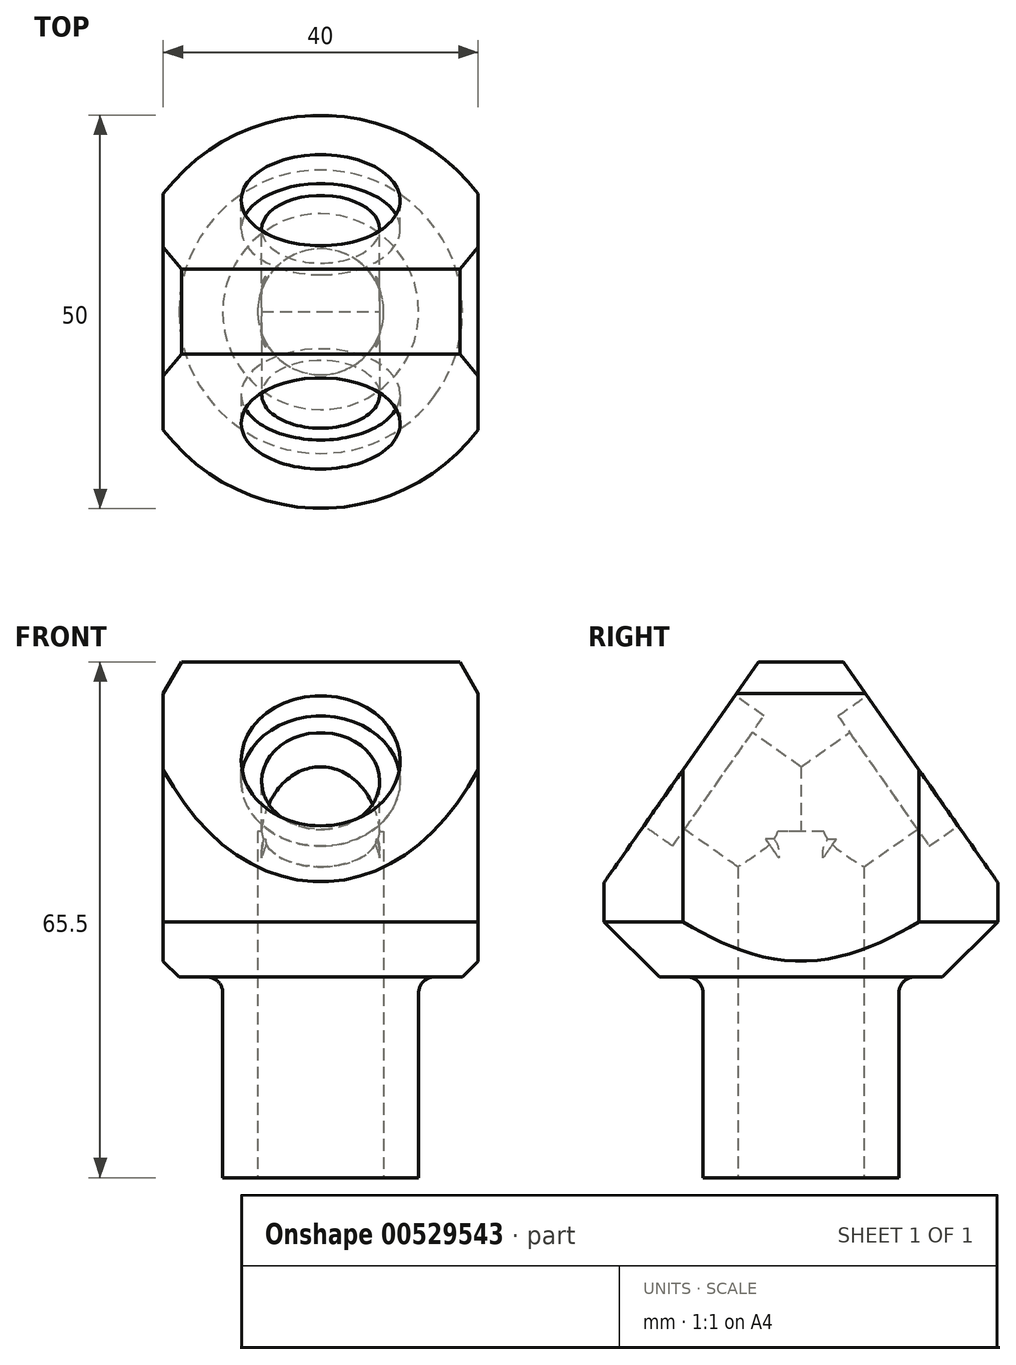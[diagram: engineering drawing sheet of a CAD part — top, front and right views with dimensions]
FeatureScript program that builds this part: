
annotation { "Feature Type Name" : "Feature", "Feature Type Description" : "" }
export const myFeature = defineFeature(function(context is Context, id is Id, definition is map)
    precondition{}
    {
        {
            var Q0;
            Q0=qCreatedBy(makeId("Top.planeOp"),FACE);
            var sketch = newSketch(context, id + "F0", { "sketchPlane" : qUnion([Q0])});
            skCircle(sketch, "E0", {"center": v(0, 0) * mm, "radius": 25 * mm});
            skSolve(sketch);
        }
        {
            var Q0;
            Q0 = qSketchRegion(id + "F0", true);
            extrude(context, id + "F1", {"entities" : qUnion([Q0]), "depth" : 65.5 * mm, "offsetDistance" : 25 * mm});
        }
        {
            var Q0;
            Q0=makeQuery(id+"F1.opExtrude","CAP_FACE",FACE,{"disambiguationData":[OSD([sQuery(id+"F0.wireOp",EDGE,"E0")])],"isStart":true});
            var sketch = newSketch(context, id + "F2", { "sketchPlane" : qUnion([Q0])});
            skCircle(sketch, "E1", {"center": v(0, 0) * mm, "radius": 8 * mm});
            skSolve(sketch);
        }
        {
            var Q0;
            Q0 = qSketchRegion(id + "F2", true);
            extrude(context, id + "F3", {"entities" : qUnion([Q0]), "operationType" : NewBodyOperationType.REMOVE, "oppositeDirection" : true, "depth" : 44 * mm, "offsetDistance" : 25 * mm});
        }
        {
            var Q0;
            Q0=qCreatedBy(makeId("Front.planeOp"),FACE);
            var sketch = newSketch(context, id + "F4", { "sketchPlane" : qUnion([Q0])});
            skLineSegment(sketch, "E2.bottom", {"start": v(37.7, 87.8) * mm, "end": v(20, 87.8) * mm});
            skLineSegment(sketch, "E2.top", {"start": v(37.7, 24) * mm, "end": v(20, 24) * mm});
            skLineSegment(sketch, "E2.left", {"start": v(37.7, 87.8) * mm, "end": v(37.7, 24) * mm});
            skLineSegment(sketch, "E2.right", {"start": v(20, 87.8) * mm, "end": v(20, 24) * mm});
            skLineSegment(sketch, "E3.bottom", {"start": v(-20, 73.43) * mm, "end": v(-40.98, 73.43) * mm});
            skLineSegment(sketch, "E3.top", {"start": v(-20, 24) * mm, "end": v(-40.98, 24) * mm});
            skLineSegment(sketch, "E3.left", {"start": v(-20, 73.43) * mm, "end": v(-20, 24) * mm});
            skLineSegment(sketch, "E3.right", {"start": v(-40.98, 73.43) * mm, "end": v(-40.98, 24) * mm});
            skSolve(sketch);
        }
        {
            var Q0;
            Q0 = qSketchRegion(id + "F4", true);
            extrude(context, id + "F5", {"entities" : qUnion([Q0]), "operationType" : NewBodyOperationType.REMOVE, "endBound" : BoundingType.SYMMETRIC, "oppositeDirection" : true, "depth" : 98.6 * mm, "offsetDistance" : 25 * mm});
        }
        {
            var Q0;
            Q0=makeQuery(id+"F5.boolean.opBoolean","INTERSECT",EDGE,{"derivedFrom":[makeQuery(id+"F1.opExtrude","CAP_FACE",FACE,{"disambiguationData":[OSD([sQuery(id+"F0.wireOp",EDGE,"E0")])],"isStart":false}),makeQuery(id+"F5.opExtrude","SWEPT_FACE",FACE,{"disambiguationData":[OSD([sQuery(id+"F4.wireOp",EDGE,"E2.right")])]})]});
            var Q1;
            Q1=makeQuery(id+"F5.boolean.opBoolean","INTERSECT",EDGE,{"derivedFrom":[makeQuery(id+"F1.opExtrude","CAP_FACE",FACE,{"disambiguationData":[OSD([sQuery(id+"F0.wireOp",EDGE,"E0")])],"isStart":false}),makeQuery(id+"F5.opExtrude","SWEPT_FACE",FACE,{"disambiguationData":[OSD([sQuery(id+"F4.wireOp",EDGE,"E3.left")])]})]});
            chamfer(context, id + "F6", {"entities" : qUnion([Q0, Q1]), "chamferType" : ChamferType.OFFSET_ANGLE, "width" : 4 * mm, "oppositeDirection" : false, "angle" : 30 * degree, "tangentPropagation" : true});
        }
        {
            var Q0;
            Q0=makeQuery(id+"F1.opExtrude","CAP_FACE",FACE,{"disambiguationData":[OSD([sQuery(id+"F0.wireOp",EDGE,"E0")])],"isStart":true});
            var sketch = newSketch(context, id + "F7", { "sketchPlane" : qUnion([Q0])});
            skCircle(sketch, "E4", {"center": v(0, 0) * mm, "radius": 12.45 * mm});
            skCircle(sketch, "E5", {"center": v(0, 0) * mm, "radius": 27.63 * mm});
            skSolve(sketch);
        }
        {
            var Q0;
            Q0 = qSketchRegion(id + "F7", true);
            extrude(context, id + "F8", {"entities" : qUnion([Q0]), "operationType" : NewBodyOperationType.REMOVE, "oppositeDirection" : true, "depth" : 25.5 * mm, "offsetDistance" : 25 * mm});
        }
        {
            var Q0;
            Q0=makeQuery(id+"F8.boolean.opBoolean","COPY",EDGE,{"derivedFrom":makeQuery(id+"F8.opExtrude","CAP_EDGE",EDGE,{"disambiguationData":[OSD([sQuery(id+"F7.wireOp",EDGE,"E4")])],"isStart":false})});
            fillet(context, id + "F9", {"entities" : qUnion([Q0]), "radius" : 2 * mm, "tangentPropagation" : true, "allowEdgeOverflow" : false});
        }
        {
            var Q0;
            Q0=qCreatedBy(makeId("Right.planeOp"),FACE);
            var sketch = newSketch(context, id + "F10", { "sketchPlane" : qUnion([Q0])});
            skLineSegment(sketch, "E6", {"start": v(14, 53.2) * mm, "end": v(2.8, 69.22) * mm});
            skLineSegment(sketch, "E7", {"start": v(2.8, 69.22) * mm, "end": v(27.83, 33.47) * mm});
            skLineSegment(sketch, "E8", {"start": v(27.83, 33.47) * mm, "end": v(27.83, 71.21) * mm});
            skLineSegment(sketch, "E9", {"start": v(27.83, 71.21) * mm, "end": v(2.8, 69.22) * mm});
            skLineSegment(sketch, "E10", {"start": v(-14, 53.2) * mm, "end": v(-2.03, 70.32) * mm});
            skLineSegment(sketch, "E11", {"start": v(-2.03, 70.32) * mm, "end": v(-28.7, 32.24) * mm});
            skLineSegment(sketch, "E12", {"start": v(-28.7, 32.24) * mm, "end": v(-27.2, 71.71) * mm});
            skLineSegment(sketch, "E13", {"start": v(-27.2, 71.71) * mm, "end": v(-2.03, 70.32) * mm});
            skSolve(sketch);
        }
        {
            var Q0;
            Q0 = qSketchRegion(id + "F10", true);
            extrude(context, id + "F11", {"entities" : qUnion([Q0]), "operationType" : NewBodyOperationType.REMOVE, "endBound" : BoundingType.SYMMETRIC, "oppositeDirection" : true, "depth" : 88.6 * mm, "offsetDistance" : 25 * mm});
        }
        {
            var Q0;
            Q0=makeQuery(id+"F8.boolean.opBoolean","INTERSECT",EDGE,{"disambiguationData":[OD(0.0)],"derivedFrom":[makeQuery(id+"F1.opExtrude","SWEPT_FACE",FACE,{"disambiguationData":[OSD([sQuery(id+"F0.wireOp",EDGE,"E0")])]}),makeQuery(id+"F8.opExtrude","CAP_FACE",FACE,{"disambiguationData":[OSD([sQuery(id+"F7.wireOp",EDGE,"E4"),sQuery(id+"F7.wireOp",EDGE,"E5")])],"isStart":false})]});
            chamfer(context, id + "F12", {"entities" : qUnion([Q0]), "width" : 7 * mm, "tangentPropagation" : true});
        }
        {
            var Q0;
            Q0=makeQuery(id+"F11.boolean.opBoolean","COPY",FACE,{"derivedFrom":makeQuery(id+"F11.opExtrude","SWEPT_FACE",FACE,{"disambiguationData":[OSD([sQuery(id+"F10.wireOp",EDGE,"E11")])]})});
            var sketch = newSketch(context, id + "F13", { "sketchPlane" : qUnion([Q0])});
            skCircle(sketch, "E14", {"center": v(0, 35.26) * mm, "radius": 10.1 * mm});
            skSolve(sketch);
        }
        {
            var Q0;
            Q0 = qSketchRegion(id + "F13", true);
            extrude(context, id + "F14", {"entities" : qUnion([Q0]), "operationType" : NewBodyOperationType.REMOVE, "oppositeDirection" : true, "depth" : 4.5 * mm, "offsetDistance" : 25 * mm});
        }
        {
            var Q0;
            Q0=makeQuery(id+"F11.boolean.opBoolean","COPY",FACE,{"derivedFrom":makeQuery(id+"F11.opExtrude","SWEPT_FACE",FACE,{"disambiguationData":[OSD([sQuery(id+"F10.wireOp",EDGE,"E7")])]})});
            var sketch = newSketch(context, id + "F15", { "sketchPlane" : qUnion([Q0])});
            skCircle(sketch, "E15", {"center": v(0, 35.26) * mm, "radius": 10.1 * mm});
            skPoint(sketch, "E15.centerSnap0", {"position": v(0, 50.56) * mm});
            skSolve(sketch);
        }
        {
            var Q0;
            Q0 = qSketchRegion(id + "F15", true);
            extrude(context, id + "F16", {"entities" : qUnion([Q0]), "operationType" : NewBodyOperationType.REMOVE, "oppositeDirection" : true, "depth" : 4.5 * mm, "offsetDistance" : 25 * mm});
        }
        {
            var Q0;
            Q0=makeQuery(id+"F16.boolean.opBoolean","COPY",FACE,{"derivedFrom":makeQuery(id+"F16.opExtrude","CAP_FACE",FACE,{"disambiguationData":[OSD([sQuery(id+"F15.wireOp",EDGE,"E15")])],"isStart":false})});
            var sketch = newSketch(context, id + "F17", { "sketchPlane" : qUnion([Q0])});
            skCircle(sketch, "E16", {"center": v(0, 35.26) * mm, "radius": 7.5 * mm});
            skSolve(sketch);
        }
        {
            var Q0;
            Q0 = qSketchRegion(id + "F17", true);
            extrude(context, id + "F18", {"entities" : qUnion([Q0]), "operationType" : NewBodyOperationType.REMOVE, "oppositeDirection" : true, "depth" : 16.5 * mm, "offsetDistance" : 25 * mm});
        }
        {
            var Q0;
            Q0=makeQuery(id+"F14.boolean.opBoolean","COPY",FACE,{"derivedFrom":makeQuery(id+"F14.opExtrude","CAP_FACE",FACE,{"disambiguationData":[OSD([sQuery(id+"F13.wireOp",EDGE,"E14")])],"isStart":false})});
            var sketch = newSketch(context, id + "F19", { "sketchPlane" : qUnion([Q0])});
            skCircle(sketch, "E17", {"center": v(0, 35.26) * mm, "radius": 7.5 * mm});
            skSolve(sketch);
        }
        {
            var Q0;
            Q0 = qSketchRegion(id + "F19", true);
            extrude(context, id + "F20", {"entities" : qUnion([Q0]), "operationType" : NewBodyOperationType.REMOVE, "oppositeDirection" : true, "depth" : 16.5 * mm, "offsetDistance" : 25 * mm});
        }
    });
